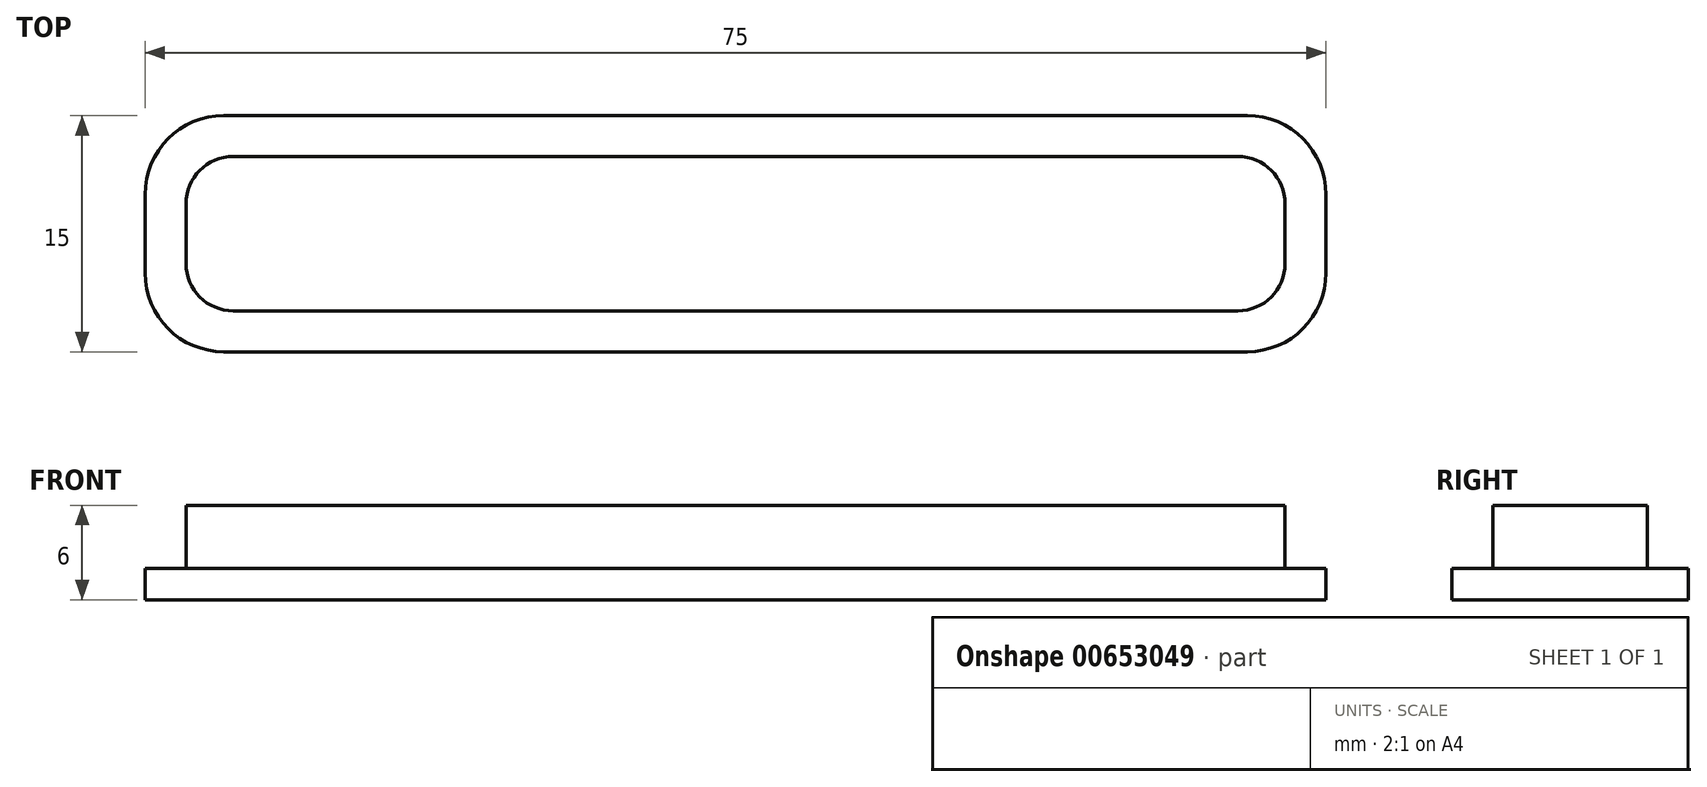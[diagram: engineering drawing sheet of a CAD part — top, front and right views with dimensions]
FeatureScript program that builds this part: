
annotation { "Feature Type Name" : "Feature", "Feature Type Description" : "" }
export const myFeature = defineFeature(function(context is Context, id is Id, definition is map)
    precondition{}
    {
        {
            var Q0;
            Q0=qCreatedBy(makeId("Top.planeOp"),FACE);
            var sketch = newSketch(context, id + "F0", { "sketchPlane" : qUnion([Q0])});
            skLineSegment(sketch, "E0.0", {"start": v(-2.86, 7.24) * mm, "end": v(72.14, 7.24) * mm});
            skLineSegment(sketch, "E0.1", {"start": v(-2.86, -7.76) * mm, "end": v(-2.86, 7.24) * mm});
            skLineSegment(sketch, "E0.2", {"start": v(-2.86, -7.76) * mm, "end": v(72.14, -7.76) * mm});
            skLineSegment(sketch, "E0.3", {"start": v(72.14, -7.76) * mm, "end": v(72.14, 7.24) * mm});
            skSolve(sketch);
        }
        {
            var Q0;
            Q0 = qSketchRegion(id + "F0", true);
            extrude(context, id + "F1", {"entities" : qUnion([Q0]), "depth" : 2 * mm, "offsetDistance" : 25 * mm});
        }
        {
            var Q0;
            Q0=makeQuery(id+"F1.opExtrude","CAP_FACE",FACE,{"disambiguationData":[OSD([sQuery(id+"F0.wireOp",EDGE,"E0.0"),sQuery(id+"F0.wireOp",EDGE,"E0.1"),sQuery(id+"F0.wireOp",EDGE,"E0.2"),sQuery(id+"F0.wireOp",EDGE,"E0.3")])],"isStart":false});
            var sketch = newSketch(context, id + "F2", { "sketchPlane" : qUnion([Q0])});
            skLineSegment(sketch, "E1.0", {"start": v(-0.26, -5.16) * mm, "end": v(69.54, -5.16) * mm});
            skLineSegment(sketch, "E1.1", {"start": v(-0.26, 4.64) * mm, "end": v(-0.26, -5.16) * mm});
            skLineSegment(sketch, "E1.2", {"start": v(69.54, 4.64) * mm, "end": v(-0.26, 4.64) * mm});
            skLineSegment(sketch, "E1.3", {"start": v(69.54, -5.16) * mm, "end": v(69.54, 4.64) * mm});
            skSolve(sketch);
        }
        {
            var Q0;
            Q0=makeQuery(id+"F2.imprint","IMPRINT",FACE,{"disambiguationData":[TD([[makeQuery(id+"F2.imprint","IMPRINT",EDGE,{"derivedFrom":sQuery(id+"F2.wireOp",EDGE,"E1.0")}),1.0]])]});
            extrude(context, id + "F3", {"entities" : qUnion([Q0]), "operationType" : NewBodyOperationType.ADD, "depth" : 4 * mm, "offsetDistance" : 25 * mm});
        }
        {
            var Q0;
            Q0=makeQuery(id+"F1.opExtrude","SWEPT_EDGE",EDGE,{"disambiguationData":[OSD([sQuery(id+"F0.wireOp",EDGE,"E0.1"),sQuery(id+"F0.wireOp",EDGE,"E0.2")])]});
            fillet(context, id + "F4", {"entities" : qUnion([Q0]), "radius" : 5 * mm, "tangentPropagation" : true, "allowEdgeOverflow" : false});
        }
        {
            var Q0;
            Q0=makeQuery(id+"F3.opExtrude","SWEPT_EDGE",EDGE,{"disambiguationData":[OSD([sQuery(id+"F2.wireOp",EDGE,"E1.0"),sQuery(id+"F2.wireOp",EDGE,"E1.1")])]});
            fillet(context, id + "F5", {"entities" : qUnion([Q0]), "radius" : 3 * mm, "tangentPropagation" : true, "allowEdgeOverflow" : false});
        }
        {
            var Q0;
            Q0=makeQuery(id+"F1.opExtrude","SWEPT_EDGE",EDGE,{"disambiguationData":[OSD([sQuery(id+"F0.wireOp",EDGE,"E0.0"),sQuery(id+"F0.wireOp",EDGE,"E0.3")])]});
            fillet(context, id + "F6", {"entities" : qUnion([Q0]), "radius" : 5 * mm, "tangentPropagation" : true, "allowEdgeOverflow" : false});
        }
        {
            var Q0;
            Q0=makeQuery(id+"F1.opExtrude","SWEPT_EDGE",EDGE,{"disambiguationData":[OSD([sQuery(id+"F0.wireOp",EDGE,"E0.2"),sQuery(id+"F0.wireOp",EDGE,"E0.3")])]});
            fillet(context, id + "F7", {"entities" : qUnion([Q0]), "radius" : 5 * mm, "tangentPropagation" : true, "allowEdgeOverflow" : false});
        }
        {
            var Q0;
            Q0=makeQuery(id+"F3.opExtrude","SWEPT_EDGE",EDGE,{"disambiguationData":[OSD([sQuery(id+"F2.wireOp",EDGE,"E1.2"),sQuery(id+"F2.wireOp",EDGE,"E1.3")])]});
            fillet(context, id + "F8", {"entities" : qUnion([Q0]), "radius" : 3 * mm, "tangentPropagation" : true, "allowEdgeOverflow" : false});
        }
        {
            var Q0;
            Q0=makeQuery(id+"F3.opExtrude","SWEPT_EDGE",EDGE,{"disambiguationData":[OSD([sQuery(id+"F2.wireOp",EDGE,"E1.0"),sQuery(id+"F2.wireOp",EDGE,"E1.3")])]});
            fillet(context, id + "F9", {"entities" : qUnion([Q0]), "radius" : 3 * mm, "tangentPropagation" : true, "allowEdgeOverflow" : false});
        }
        {
            var Q0;
            Q0=makeQuery(id+"F1.opExtrude","SWEPT_EDGE",EDGE,{"disambiguationData":[OSD([sQuery(id+"F0.wireOp",EDGE,"E0.0"),sQuery(id+"F0.wireOp",EDGE,"E0.1")])]});
            fillet(context, id + "F10", {"entities" : qUnion([Q0]), "radius" : 5 * mm, "tangentPropagation" : true, "allowEdgeOverflow" : false});
        }
        {
            var Q0;
            Q0=makeQuery(id+"F3.opExtrude","SWEPT_EDGE",EDGE,{"disambiguationData":[OSD([sQuery(id+"F2.wireOp",EDGE,"E1.1"),sQuery(id+"F2.wireOp",EDGE,"E1.2")])]});
            fillet(context, id + "F11", {"entities" : qUnion([Q0]), "radius" : 3 * mm, "tangentPropagation" : true, "allowEdgeOverflow" : false});
        }
    });
